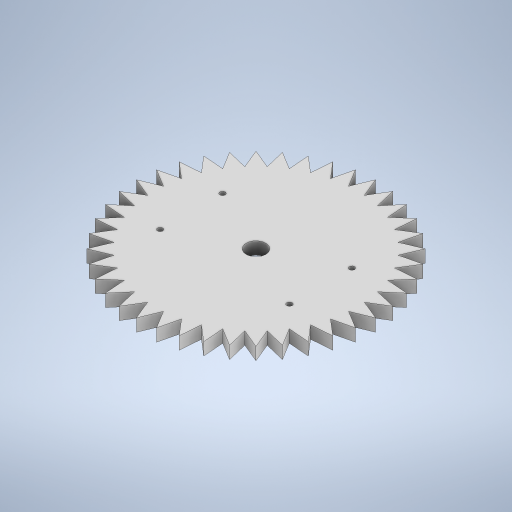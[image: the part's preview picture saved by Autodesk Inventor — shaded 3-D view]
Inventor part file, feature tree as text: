
AUTODESK INVENTOR PART (.ipt)
format: ipt  version: 2023 (Build 270158030, 158C)  size: 315,392 bytes
history: native  units: in
note: dims shown in document units (in); Inventor stores cm internally (conversion verified against a paired STEP export)
features: sketch x4, extrude x3, pattern_circular x1, hole x1
ambient origin geometry x8: Origin, YZ Plane, XZ Plane, XY Plane, X Axis, Y Axis, Z Axis, Center Point
bodies: Solid1 (feature_tree)
feature tree (9):
  extrude  "Extrusion1"  Depth=0.5in TaperAngle=0.0deg
  extrude  "Extrusion2"  Depth=0.7874in
  pattern_circular  "Circular Pattern1"  Count=40 Angle=360.0deg
  extrude  "Extrusion3"  Depth=0.3937in TaperAngle=0.0deg
  hole  "Hole1"  [1 undecoded]
  sketch  "Sketch1"  dims[d0=8.0in d1=0.5in d2=0.0in]
  sketch  "Sketch2"  dims[d3=45.0deg d4=0.7874in]
  sketch  "Sketch3"  dims[d5=0.0in d6=0.0in d7=15.748in d8=360.0deg]
  sketch  "Sketch5"  dims[d10=0.7874in d11=0.3937in d12=0.0in d15=0.2165in d16=0.2362in d17=0.1417in d18=0.0787in d19=90.0deg d20=0.315in d21=0.8108in d22=2.5in d23=5.18in]
note: 1 required parameter value undecoded (feature->parameter linkage not recoverable at this tier; creation-order binding heuristic only, values carry confidence <= 0.55)
